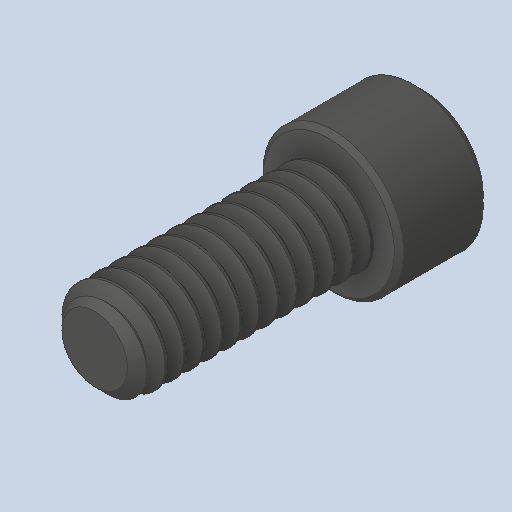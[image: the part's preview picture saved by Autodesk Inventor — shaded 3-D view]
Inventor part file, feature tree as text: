
AUTODESK INVENTOR PART (.ipt)
format: ipt  version: 2023 (Build 270158000, 158)  size: 532,992 bytes
history: native  units: in
note: dims shown in document units (in); Inventor stores cm internally (conversion verified against a paired STEP export)
features: chamfer x1
ambient origin geometry x8: Origin, YZ Plane, XZ Plane, XY Plane, X Axis, Y Axis, Z Axis, Center Point
bodies: Solid1 (feature_tree)
feature tree (1):
  chamfer  "Chamfer2"  [1 undecoded]
note: 1 required parameter value undecoded (feature->parameter linkage not recoverable at this tier; creation-order binding heuristic only, values carry confidence <= 0.55)
